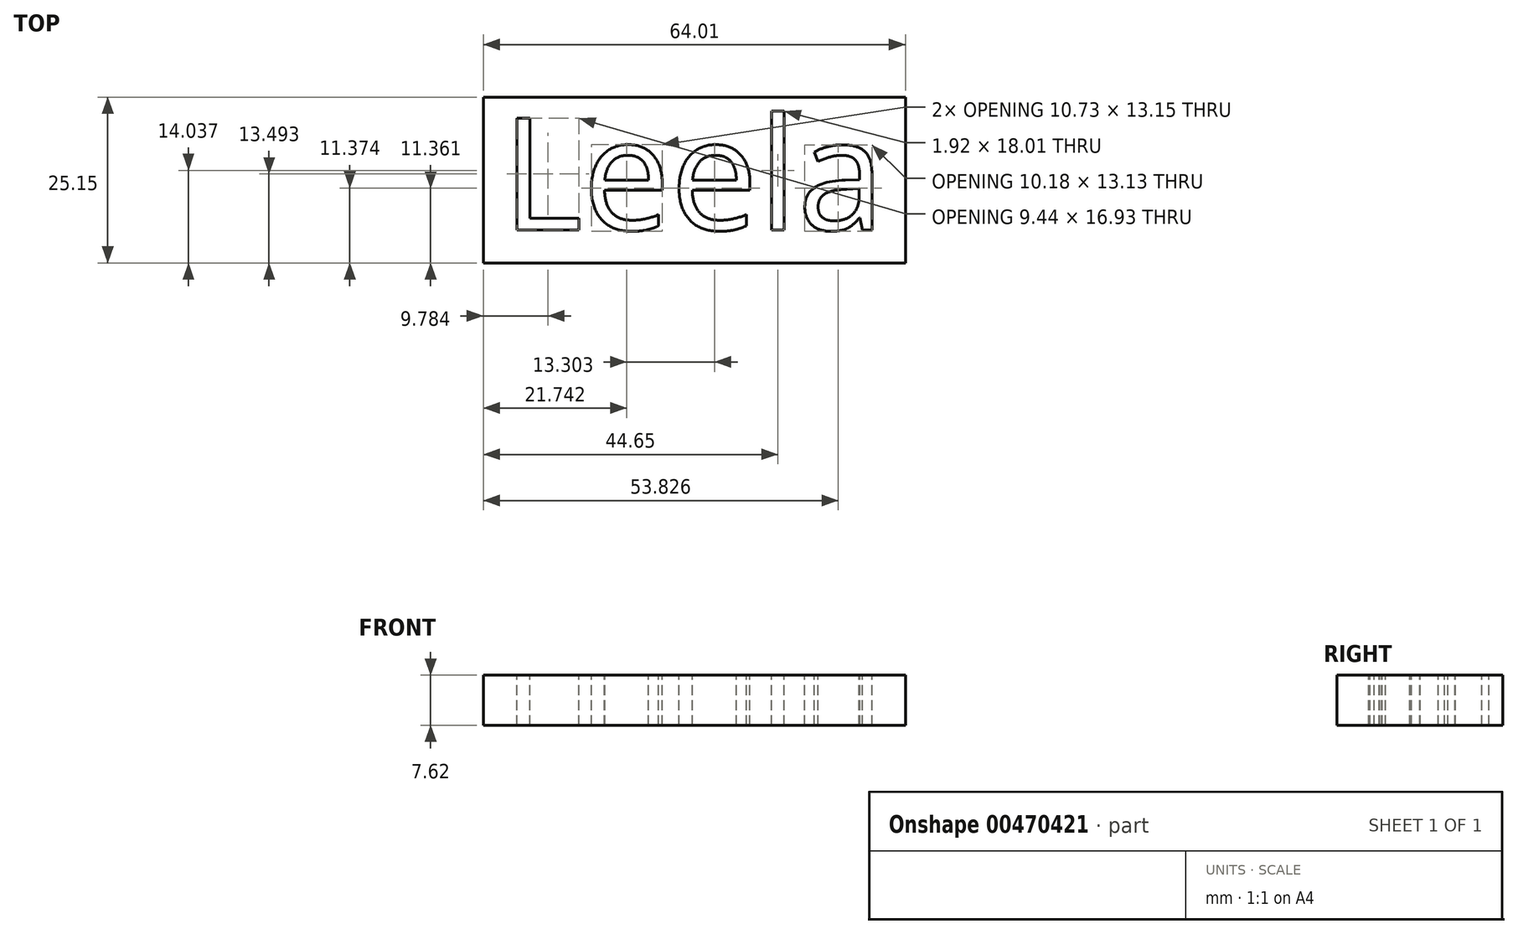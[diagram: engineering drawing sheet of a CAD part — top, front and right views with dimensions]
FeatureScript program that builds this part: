
annotation { "Feature Type Name" : "Feature", "Feature Type Description" : "" }
export const myFeature = defineFeature(function(context is Context, id is Id, definition is map)
    precondition{}
    {
        {
            var Q0;
            Q0=qCreatedBy(makeId("Top.planeOp"),FACE);
            var sketch = newSketch(context, id + "F0", { "sketchPlane" : qUnion([Q0])});
            skLineSegment(sketch, "E0.bottom", {"start": v(0, 0) * mm, "end": v(64, 0) * mm});
            skLineSegment(sketch, "E0.top", {"start": v(0, 25.15) * mm, "end": v(64, 25.15) * mm});
            skLineSegment(sketch, "E0.left", {"start": v(0, 0) * mm, "end": v(0, 25.15) * mm});
            skLineSegment(sketch, "E0.right", {"start": v(64, 0) * mm, "end": v(64, 25.15) * mm});
            skSolve(sketch);
        }
        {
            var Q0;
            Q0 = qSketchRegion(id + "F0", true);
            extrude(context, id + "F1", {"entities" : qUnion([Q0]), "depth" : 7.62 * mm});
        }
        {
            var Q0;
            Q0=makeQuery(id+"F1.opExtrude","CAP_FACE",FACE,{"disambiguationData":[OSD([sQuery(id+"F0.wireOp",EDGE,"E0.bottom"),sQuery(id+"F0.wireOp",EDGE,"E0.top"),sQuery(id+"F0.wireOp",EDGE,"E0.left"),sQuery(id+"F0.wireOp",EDGE,"E0.right")])],"isStart":false});
            var sketch = newSketch(context, id + "F2", { "sketchPlane" : qUnion([Q0])});
            skText(sketch, "E1", { "text": "Leela ", "fontName": "OpenSans-Regular.ttf"});
            const initialGuessF2  = {"E1": [0.00274, 0.00503, 1, 0, 0.01707]};
            skSetInitialGuess(sketch, initialGuessF2);
            skSolve(sketch);
        }
        {
            var Q0;
            Q0 = qSketchRegion(id + "F2", true);
            extrude(context, id + "F3", {"entities" : qUnion([Q0]), "operationType" : NewBodyOperationType.REMOVE, "endBound" : BoundingType.THROUGH_ALL, "oppositeDirection" : true, "depth" : 5.33 * mm});
        }
    });
